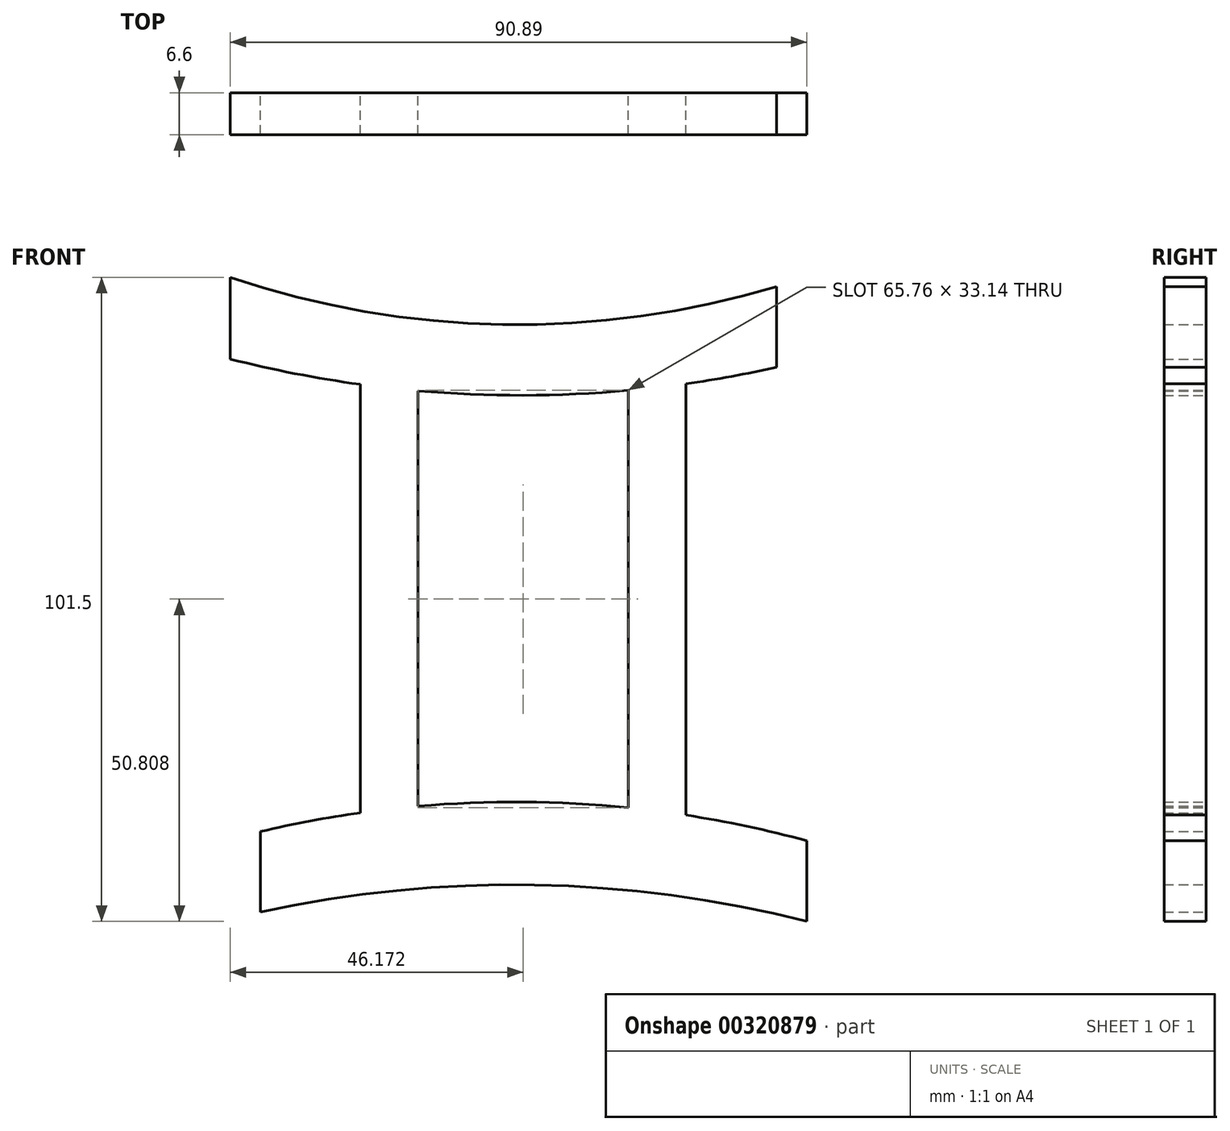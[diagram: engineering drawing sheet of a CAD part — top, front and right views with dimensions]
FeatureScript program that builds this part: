
annotation { "Feature Type Name" : "Feature", "Feature Type Description" : "" }
export const myFeature = defineFeature(function(context is Context, id is Id, definition is map)
    precondition{}
    {
        {
            var Q0;
            Q0=qCreatedBy(makeId("Front.planeOp"),FACE);
            var sketch = newSketch(context, id + "F0", { "sketchPlane" : qUnion([Q0])});
            skArc(sketch, "E0", {"start": v(42.3, -40.2) * mm, "mid": v(-0.66, -34.44) * mm, "end": v(-43.8, -38.73) * mm});
            skArc(sketch, "E1", {"start": v(-48.58, 61.3) * mm, "mid": v(-5.64, 53.88) * mm, "end": v(37.53, 59.83) * mm});
            skLineSegment(sketch, "E2", {"start": v(-48.58, 61.3) * mm, "end": v(-48.58, 48.43) * mm});
            skLineSegment(sketch, "E3", {"start": v(-43.8, -38.73) * mm, "end": v(-43.8, -26.03) * mm});
            skLineSegment(sketch, "E4", {"start": v(37.53, 59.83) * mm, "end": v(37.53, 47.13) * mm});
            skLineSegment(sketch, "E5", {"start": v(42.3, -40.2) * mm, "end": v(42.3, -27.5) * mm});
            skArc(sketch, "E6", {"start": v(42.3, -27.5) * mm, "mid": v(32.84, -25.2) * mm, "end": v(23.25, -23.44) * mm});
            skArc(sketch, "E7", {"start": v(-48.58, 48.43) * mm, "mid": v(-38.38, 46.15) * mm, "end": v(-28.07, 44.44) * mm});
            skLineSegment(sketch, "E8", {"start": v(-28.07, 44.44) * mm, "end": v(-28.07, -23.08) * mm});
            skLineSegment(sketch, "E9", {"start": v(-18.98, 43.42) * mm, "end": v(-18.98, -22.04) * mm});
            skArc(sketch, "E10.trimOffspring", {"start": v(-18.98, 43.42) * mm, "mid": v(-2.4, 42.72) * mm, "end": v(14.16, 43.49) * mm});
            skArc(sketch, "E11.trimOffspring", {"start": v(-28.07, -23.08) * mm, "mid": v(-35.97, -24.37) * mm, "end": v(-43.8, -26.03) * mm});
            skLineSegment(sketch, "E12", {"start": v(23.25, 44.54) * mm, "end": v(23.25, -23.44) * mm});
            skLineSegment(sketch, "E13", {"start": v(14.16, 43.49) * mm, "end": v(14.16, -22.27) * mm});
            skArc(sketch, "E14.trimOffspring", {"start": v(23.25, 44.54) * mm, "mid": v(30.42, 45.7) * mm, "end": v(37.53, 47.13) * mm});
            skArc(sketch, "E15.trimOffspring", {"start": v(14.16, -22.27) * mm, "mid": v(-2.4, -21.37) * mm, "end": v(-18.98, -22.04) * mm});
            skSolve(sketch);
        }
        {
            var Q0;
            Q0=makeQuery(id+"F0.imprint","IMPRINT",FACE,{"disambiguationData":[TD([[makeQuery(id+"F0.imprint","IMPRINT",EDGE,{"derivedFrom":sQuery(id+"F0.wireOp",EDGE,"E0")}),-1.0]])]});
            extrude(context, id + "F1", {"entities" : qUnion([Q0]), "depth" : 6.6 * mm});
        }
    });
